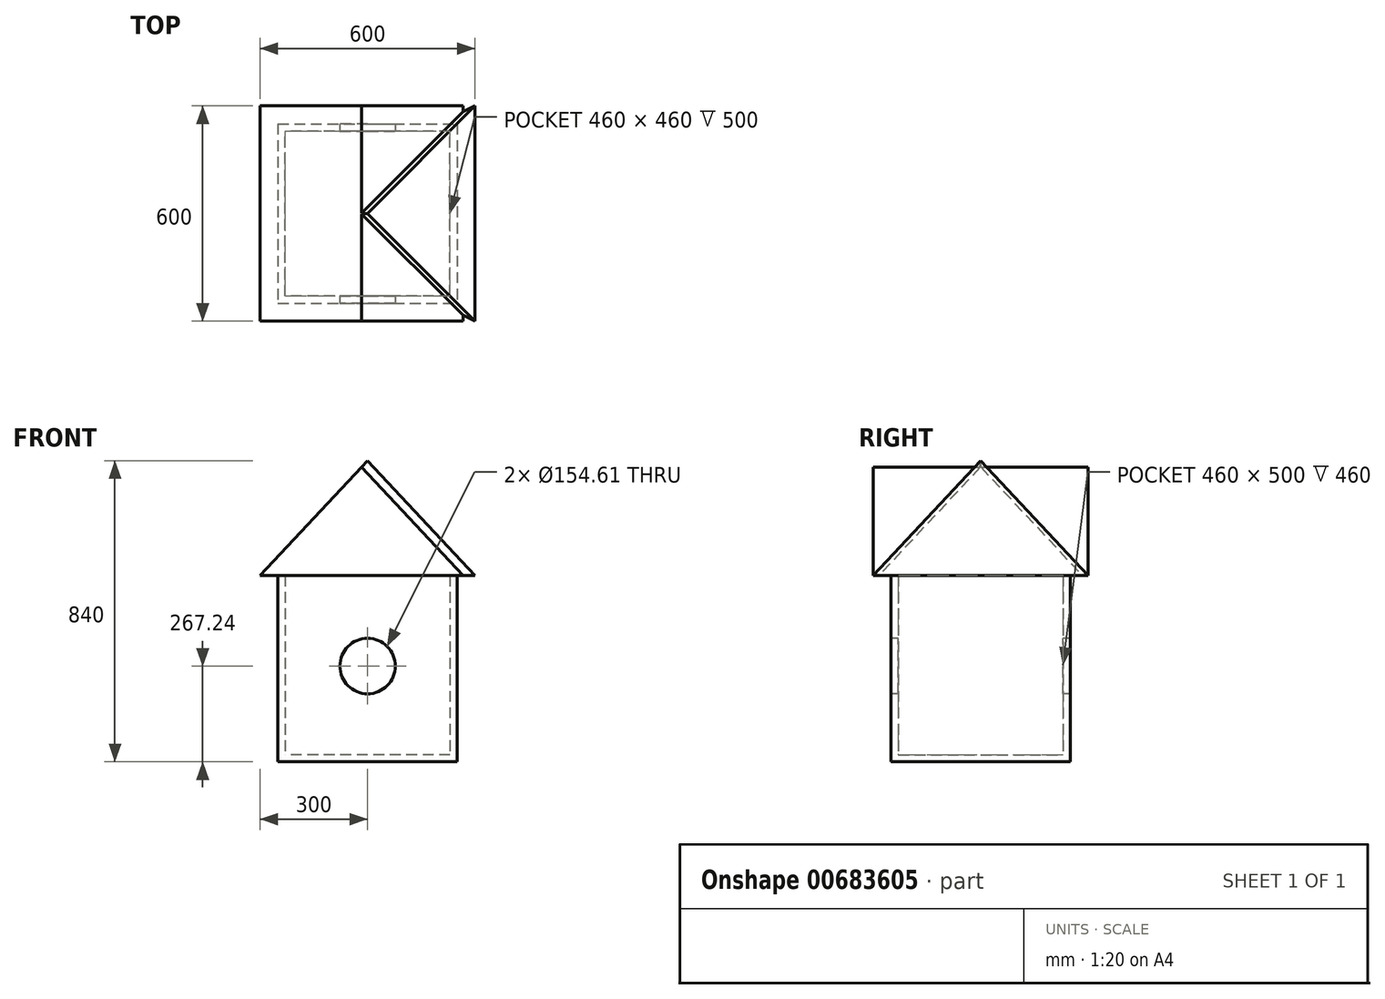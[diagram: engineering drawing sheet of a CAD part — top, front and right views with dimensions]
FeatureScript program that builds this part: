
annotation { "Feature Type Name" : "Feature", "Feature Type Description" : "" }
export const myFeature = defineFeature(function(context is Context, id is Id, definition is map)
    precondition{}
    {
        {
            var Q0;
            Q0=qCreatedBy(makeId("Top.planeOp"),FACE);
            var sketch = newSketch(context, id + "F0", { "sketchPlane" : qUnion([Q0])});
            skLineSegment(sketch, "E0.bottom", {"start": v(-250, 250) * mm, "end": v(250, 250) * mm});
            skLineSegment(sketch, "E0.top", {"start": v(-250, -250) * mm, "end": v(250, -250) * mm});
            skLineSegment(sketch, "E0.left", {"start": v(-250, 250) * mm, "end": v(-250, -250) * mm});
            skLineSegment(sketch, "E0.right", {"start": v(250, 250) * mm, "end": v(250, -250) * mm});
            skPoint(sketch, "E0.middle", {"position": v(0, 0) * mm});
            skSolve(sketch);
        }
        {
            var Q0;
            Q0 = qSketchRegion(id + "F0", true);
            extrude(context, id + "F1", {"entities" : qUnion([Q0]), "depth" : 20 * mm, "offsetDistance" : 25 * mm});
        }
        {
            var Q0;
            Q0=makeQuery(id+"F1.opExtrude","CAP_FACE",FACE,{"disambiguationData":[OSD([sQuery(id+"F0.wireOp",EDGE,"E0.bottom"),sQuery(id+"F0.wireOp",EDGE,"E0.top"),sQuery(id+"F0.wireOp",EDGE,"E0.left"),sQuery(id+"F0.wireOp",EDGE,"E0.right")])],"isStart":false});
            var sketch = newSketch(context, id + "F2", { "sketchPlane" : qUnion([Q0])});
            skLineSegment(sketch, "E1.bottom", {"start": v(230, -230) * mm, "end": v(-230, -230) * mm});
            skLineSegment(sketch, "E1.top", {"start": v(230, 230) * mm, "end": v(-230, 230) * mm});
            skLineSegment(sketch, "E1.left", {"start": v(230, -230) * mm, "end": v(230, 230) * mm});
            skLineSegment(sketch, "E1.right", {"start": v(-230, -230) * mm, "end": v(-230, 230) * mm});
            skPoint(sketch, "E1.middle", {"position": v(0, 0) * mm});
            skSolve(sketch);
        }
        {
            var Q0;
            Q0=makeQuery(id+"F2.imprint","IMPRINT",FACE,{"disambiguationData":[TD([[makeQuery(id+"F2.imprint","IMPRINT",EDGE,{"derivedFrom":sQuery(id+"F2.wireOp",EDGE,"E1.bottom")}),1.0]])]});
            extrude(context, id + "F3", {"entities" : qUnion([Q0]), "operationType" : NewBodyOperationType.ADD, "depth" : 500 * mm, "offsetDistance" : 25 * mm});
        }
        {
            var Q0;
            {var subQ0=sQuery(id+"F0.wireOp",EDGE,"E0.top");Q0=makeQuery(id+"F3.boolean.opBoolean","MERGE",FACE,{"derivedFrom":[makeQuery(id+"F1.opExtrude","SWEPT_FACE",FACE,{"disambiguationData":[OSD([subQ0])]}),makeQuery(id+"F3.opExtrude","SWEPT_FACE",FACE,{"disambiguationData":[OSD([subQ0])]})]});}
            var sketch = newSketch(context, id + "F4", { "sketchPlane" : qUnion([Q0])});
            skPoint(sketch, "E2", {"position": v(0, 267.24) * mm});
            skCircle(sketch, "E3", {"center": v(0, 267.24) * mm, "radius": 77.3 * mm});
            skSolve(sketch);
        }
        {
            var Q0;
            Q0=makeQuery(id+"F4.imprint","IMPRINT",FACE,{"disambiguationData":[TD([[makeQuery(id+"F4.imprint","IMPRINT",EDGE,{"derivedFrom":sQuery(id+"F4.wireOp",EDGE,"E3")}),1.0]])]});
            extrude(context, id + "F5", {"entities" : qUnion([Q0]), "operationType" : NewBodyOperationType.REMOVE, "endBound" : BoundingType.THROUGH_ALL, "oppositeDirection" : true, "depth" : 20 * mm, "offsetDistance" : 25 * mm});
        }
        {
            var Q0;
            Q0=makeQuery(id+"F3.opExtrude","CAP_FACE",FACE,{"disambiguationData":[OSD([sQuery(id+"F0.wireOp",EDGE,"E0.bottom"),sQuery(id+"F0.wireOp",EDGE,"E0.top"),sQuery(id+"F0.wireOp",EDGE,"E0.left"),sQuery(id+"F0.wireOp",EDGE,"E0.right"),sQuery(id+"F2.wireOp",EDGE,"E1.bottom"),sQuery(id+"F2.wireOp",EDGE,"E1.top"),sQuery(id+"F2.wireOp",EDGE,"E1.left"),sQuery(id+"F2.wireOp",EDGE,"E1.right")])],"isStart":false});
            var sketch = newSketch(context, id + "F6", { "sketchPlane" : qUnion([Q0])});
            skLineSegment(sketch, "E4.bottom", {"start": v(300, -300) * mm, "end": v(-300, -300) * mm});
            skLineSegment(sketch, "E4.top", {"start": v(300, 300) * mm, "end": v(-300, 300) * mm});
            skLineSegment(sketch, "E4.left", {"start": v(300, -300) * mm, "end": v(300, 300) * mm});
            skLineSegment(sketch, "E4.right", {"start": v(-300, -300) * mm, "end": v(-300, 300) * mm});
            skPoint(sketch, "E4.middle", {"position": v(0, 0) * mm});
            skSolve(sketch);
        }
        {
            var Q0;
            Q0 = qSketchRegion(id + "F6", true);
            extrude(context, id + "F7", {"entities" : qUnion([Q0]), "operationType" : NewBodyOperationType.ADD, "depth" : 20 * mm, "offsetDistance" : 25 * mm});
        }
        {
            var Q0;
            Q0=makeQuery(id+"F7.opExtrude","CAP_FACE",FACE,{"disambiguationData":[OSD([sQuery(id+"F6.wireOp",EDGE,"E4.bottom"),sQuery(id+"F6.wireOp",EDGE,"E4.top"),sQuery(id+"F6.wireOp",EDGE,"E4.left"),sQuery(id+"F6.wireOp",EDGE,"E4.right")])],"isStart":false});
            extrude(context, id + "F8", {"entities" : qUnion([Q0]), "operationType" : NewBodyOperationType.ADD, "depth" : 300 * mm, "offsetDistance" : 25 * mm});
        }
        {
            var Q0;
            {var subQ0=sQuery(id+"F6.wireOp",EDGE,"E4.bottom");Q0=makeQuery(id+"F8.boolean.opBoolean","MERGE",FACE,{"derivedFrom":[makeQuery(id+"F7.opExtrude","SWEPT_FACE",FACE,{"disambiguationData":[OSD([subQ0])]}),makeQuery(id+"F8.opExtrude","SWEPT_FACE",FACE,{"disambiguationData":[OSD([subQ0])]})]});}
            var sketch = newSketch(context, id + "F9", { "sketchPlane" : qUnion([Q0])});
            skPoint(sketch, "E5", {"position": v(0, 840) * mm});
            skLineSegment(sketch, "E6", {"start": v(0, 840) * mm, "end": v(-300, 520) * mm});
            skLineSegment(sketch, "E7", {"start": v(0, 840) * mm, "end": v(300, 520) * mm});
            skSolve(sketch);
        }
        {
            var Q0;
            {var subQ0=sQuery(id+"F9.wireOp",EDGE,"E6");Q0=makeQuery(id+"F9.imprint","IMPRINT",FACE,{"disambiguationData":[TD([[makeQuery(id+"F9.imprint","IMPRINT",EDGE,{"derivedFrom":subQ0}),-1.0]])]});}
            var Q1;
            {var subQ0=sQuery(id+"F9.wireOp",EDGE,"E7");Q1=makeQuery(id+"F9.imprint","IMPRINT",FACE,{"disambiguationData":[TD([[makeQuery(id+"F9.imprint","IMPRINT",EDGE,{"derivedFrom":subQ0}),1.0]])]});}
            extrude(context, id + "F10", {"entities" : qUnion([Q0, Q1]), "operationType" : NewBodyOperationType.REMOVE, "endBound" : BoundingType.THROUGH_ALL, "oppositeDirection" : true, "depth" : 600 * mm, "offsetDistance" : 25 * mm});
        }
        {
            var Q0;
            Q0=makeQuery(id+"F10.boolean.opBoolean","COPY",FACE,{"derivedFrom":makeQuery(id+"F10.opExtrude","SWEPT_FACE",FACE,{"disambiguationData":[OSD([sQuery(id+"F9.wireOp",EDGE,"E7")])]})});
            var sketch = newSketch(context, id + "F11", { "sketchPlane" : qUnion([Q0])});
            skPoint(sketch, "E8", {"position": v(0, 612.81) * mm});
            skLineSegment(sketch, "E9", {"start": v(0, 612.81) * mm, "end": v(-300, 174.18) * mm});
            skLineSegment(sketch, "E10", {"start": v(0, 612.81) * mm, "end": v(300, 174.18) * mm});
            skSolve(sketch);
        }
        {
            var Q0;
            {var subQ0=sQuery(id+"F11.wireOp",EDGE,"E9");Q0=makeQuery(id+"F11.imprint","IMPRINT",FACE,{"disambiguationData":[TD([[makeQuery(id+"F11.imprint","IMPRINT",EDGE,{"derivedFrom":subQ0}),-1.0]])]});}
            var Q1;
            {var subQ0=sQuery(id+"F11.wireOp",EDGE,"E10");Q1=makeQuery(id+"F11.imprint","IMPRINT",FACE,{"disambiguationData":[TD([[makeQuery(id+"F11.imprint","IMPRINT",EDGE,{"derivedFrom":subQ0}),1.0]])]});}
            extrude(context, id + "F12", {"entities" : qUnion([Q0, Q1]), "operationType" : NewBodyOperationType.REMOVE, "oppositeDirection" : true, "depth" : 25 * mm, "offsetDistance" : 25 * mm});
        }
    });
